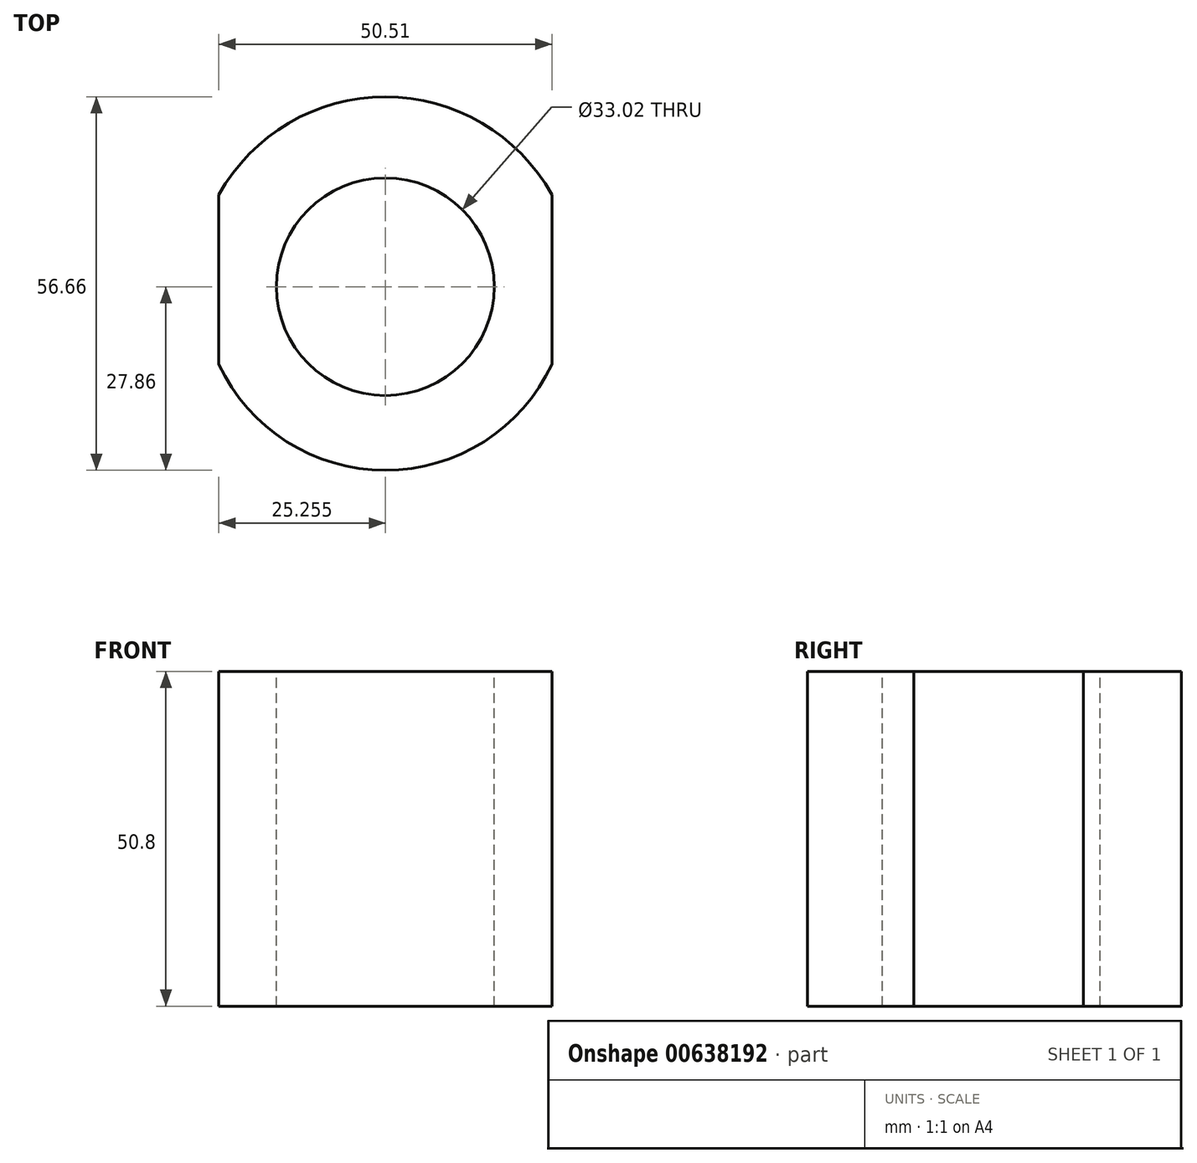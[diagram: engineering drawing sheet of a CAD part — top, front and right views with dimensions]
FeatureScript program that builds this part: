
annotation { "Feature Type Name" : "Feature", "Feature Type Description" : "" }
export const myFeature = defineFeature(function(context is Context, id is Id, definition is map)
    precondition{}
    {
        {
            var Q0;
            Q0=qCreatedBy(makeId("Top.planeOp"),FACE);
            var sketch = newSketch(context, id + "F0", { "sketchPlane" : qUnion([Q0])});
            skArc(sketch, "E0", {"start": v(29.74, 0) * mm, "mid": v(4.48, 14.85) * mm, "end": v(-20.77, 0) * mm});
            skLineSegment(sketch, "E1", {"start": v(-20.77, 0) * mm, "end": v(-20.77, -25.72) * mm});
            skLineSegment(sketch, "E2", {"start": v(29.74, -25.72) * mm, "end": v(29.74, 0) * mm});
            skArc(sketch, "E3", {"start": v(-20.77, -25.72) * mm, "mid": v(4.48, -41.81) * mm, "end": v(29.74, -25.72) * mm});
            skSolve(sketch);
        }
        {
            var Q0;
            Q0=makeQuery(id+"F0.imprint","IMPRINT",FACE,{"disambiguationData":[TD([[makeQuery(id+"F0.imprint","IMPRINT",EDGE,{"derivedFrom":sQuery(id+"F0.wireOp",EDGE,"E0")}),1.0]])]});
            extrude(context, id + "F1", {"entities" : qUnion([Q0]), "depth" : 50.8 * mm, "offsetDistance" : 25.4 * mm});
        }
        {
            var Q0;
            Q0=makeQuery(id+"F1.opExtrude","CAP_FACE",FACE,{"disambiguationData":[OSD([sQuery(id+"F0.wireOp",EDGE,"E0"),sQuery(id+"F0.wireOp",EDGE,"E1"),sQuery(id+"F0.wireOp",EDGE,"E2"),sQuery(id+"F0.wireOp",EDGE,"E3")])],"isStart":false});
            var sketch = newSketch(context, id + "F2", { "sketchPlane" : qUnion([Q0])});
            skCircle(sketch, "E4", {"center": v(4.48, -13.95) * mm, "radius": 5.09 * mm});
            skSolve(sketch);
        }
        {
            var Q0;
            Q0=sQuery(id+"F2.wireOp",VERTEX,"E4.center");
            var Q1;
            Q1=makeQuery(id+"F1.opExtrude","SWEPT_BODY",BODY,{"disambiguationData":[OSD([sQuery(id+"F0.wireOp",EDGE,"E0"),sQuery(id+"F0.wireOp",EDGE,"E1"),sQuery(id+"F0.wireOp",EDGE,"E2"),sQuery(id+"F0.wireOp",EDGE,"E3")])]});
            hole(context, id + "F3", {"style" : HoleStyle.SIMPLE, "endStyle" : HoleEndStyle.THROUGH, "holeDiameter" : 33.02 * mm, "majorDiameter" : 6.35 * mm, "isTappedThrough" : true, "tappedDepth" : 12.7 * mm, "tapClearance" : 3, "locations" : qUnion([Q0]), "scope" : qUnion([Q1])});
        }
    });
